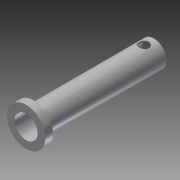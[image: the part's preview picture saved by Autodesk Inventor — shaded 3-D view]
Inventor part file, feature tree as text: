
AUTODESK INVENTOR PART (.ipt)
format: ipt  version: 2013 (Build 170138000, 138)  size: 108,544 bytes
history: native  units: in
note: dims shown in document units (in); Inventor stores cm internally (conversion verified against a paired STEP export)
features: sketch x4, extrude x3, plane x2
ambient origin geometry x8: Origin, YZ Plane, XZ Plane, XY Plane, X Axis, Y Axis, Z Axis, Center Point
bodies: Solid1 (feature_tree)
feature tree (9):
  extrude  "Extrusion1"  Depth=0.45in
  extrude  "Extrusion2"  Depth=0.75in
  sketch  "Sketch3"  dims[d5=0.15in d6=0.0in d7=90.0deg d8=0.25in]
  plane  "Work Plane2"
  extrude  "Extrusion3"  Depth=0.25in TaperAngle=90.0deg
  sketch  "Sketch1"  dims[d0=0.5in d1=0.45in]
  sketch  "Sketch2"  dims[d2=2.5in d3=0.0in d4=0.75in]
  plane  "Work Plane1"
  sketch  "Sketch4"  dims[d9=0.2in d10=0.2in d11=2.0in d12=0.0in]
